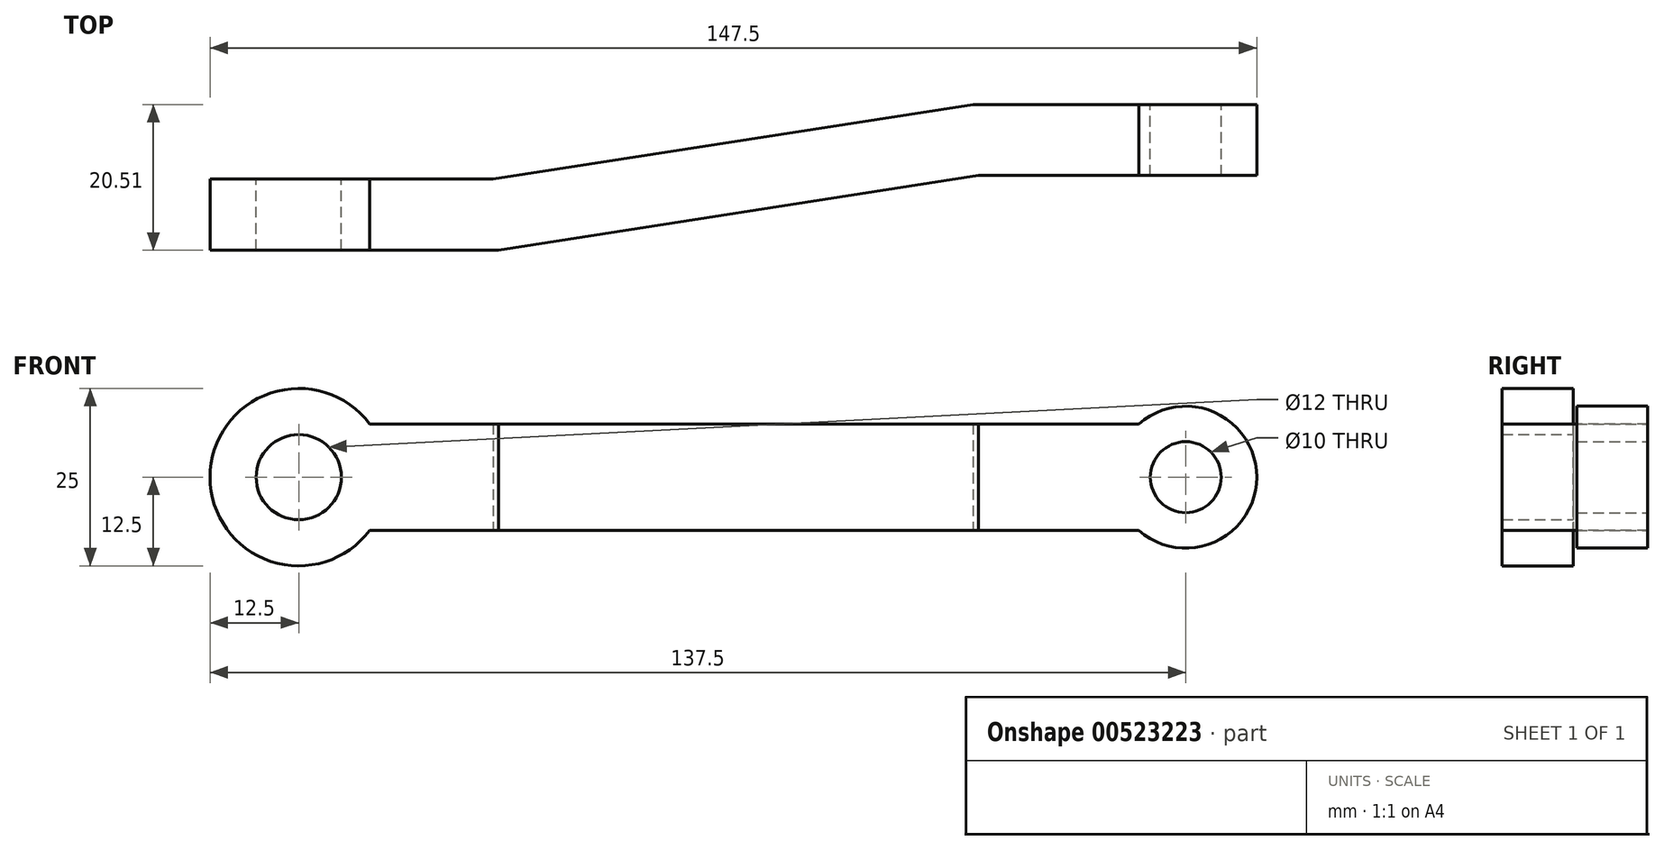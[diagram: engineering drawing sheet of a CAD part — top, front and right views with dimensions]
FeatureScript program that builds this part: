
annotation { "Feature Type Name" : "Feature", "Feature Type Description" : "" }
export const myFeature = defineFeature(function(context is Context, id is Id, definition is map)
    precondition{}
    {
        {
            var Q0;
            Q0=qCreatedBy(makeId("Front.planeOp"),FACE);
            var sketch = newSketch(context, id + "F0", { "sketchPlane" : qUnion([Q0])});
            skCircle(sketch, "E0", {"center": v(0, 0) * mm, "radius": 12.5 * mm});
            skCircle(sketch, "E1", {"center": v(125, 0) * mm, "radius": 10 * mm});
            skLineSegment(sketch, "E2", {"start": v(12.5, 0) * mm, "end": v(115, 0) * mm, "construction": true});
            skLineSegment(sketch, "E3", {"start": v(10, 7.5) * mm, "end": v(118.39, 7.5) * mm});
            skLineSegment(sketch, "E4.MirrorCS", {"start": v(10, -7.5) * mm, "end": v(118.39, -7.5) * mm});
            skCircle(sketch, "E5", {"center": v(0, 0) * mm, "radius": 6 * mm});
            skCircle(sketch, "E6", {"center": v(125, 0) * mm, "radius": 5 * mm});
            skSolve(sketch);
        }
        {
            var Q0;
            {var subQ0=sQuery(id+"F0.wireOp",EDGE,"E4.MirrorCS");Q0=makeQuery(id+"F0.imprint","IMPRINT",FACE,{"disambiguationData":[TD([[makeQuery(id+"F0.imprint","IMPRINT",EDGE,{"derivedFrom":subQ0}),1.0]])]});}
            var Q1;
            Q1=makeQuery(id+"F0.imprint","IMPRINT",FACE,{"disambiguationData":[TD([[makeQuery(id+"F0.imprint","IMPRINT",EDGE,{"derivedFrom":sQuery(id+"F0.wireOp",EDGE,"E6")}),-1.0]])]});
            var Q2;
            Q2=makeQuery(id+"F0.imprint","IMPRINT",FACE,{"disambiguationData":[TD([[makeQuery(id+"F0.imprint","IMPRINT",EDGE,{"derivedFrom":sQuery(id+"F0.wireOp",EDGE,"E5")}),-1.0]])]});
            extrude(context, id + "F1", {"entities" : qUnion([Q0, Q1, Q2]), "endBound" : BoundingType.SYMMETRIC, "depth" : 25 * mm, "offsetDistance" : 25 * mm});
        }
        {
            var Q0;
            Q0=qCreatedBy(makeId("Top.planeOp"),FACE);
            var sketch = newSketch(context, id + "F2", { "sketchPlane" : qUnion([Q0])});
            skLineSegment(sketch, "E7", {"start": v(-19.64, 0) * mm, "end": v(27.4, 0) * mm});
            skLineSegment(sketch, "E8", {"start": v(27.4, 0) * mm, "end": v(95.03, 10.51) * mm});
            skLineSegment(sketch, "E9", {"start": v(95.03, 10.51) * mm, "end": v(143.51, 10.51) * mm});
            skLineSegment(sketch, "E10.0", {"start": v(95.8, 0.51) * mm, "end": v(143.51, 0.51) * mm});
            skLineSegment(sketch, "E10.1", {"start": v(28.18, -10) * mm, "end": v(95.8, 0.51) * mm});
            skLineSegment(sketch, "E10.2", {"start": v(-19.64, -10) * mm, "end": v(28.18, -10) * mm});
            skLineSegment(sketch, "E11", {"start": v(-19.64, 0) * mm, "end": v(-19.64, -10) * mm});
            skLineSegment(sketch, "E12", {"start": v(143.51, 10.51) * mm, "end": v(143.51, 0.51) * mm});
            skSolve(sketch);
        }
        {
            var Q0;
            Q0 = qSketchRegion(id + "F2", true);
            extrude(context, id + "F3", {"entities" : qUnion([Q0]), "operationType" : NewBodyOperationType.INTERSECT, "endBound" : BoundingType.SYMMETRIC, "depth" : 25 * mm, "offsetDistance" : 25 * mm});
        }
    });
